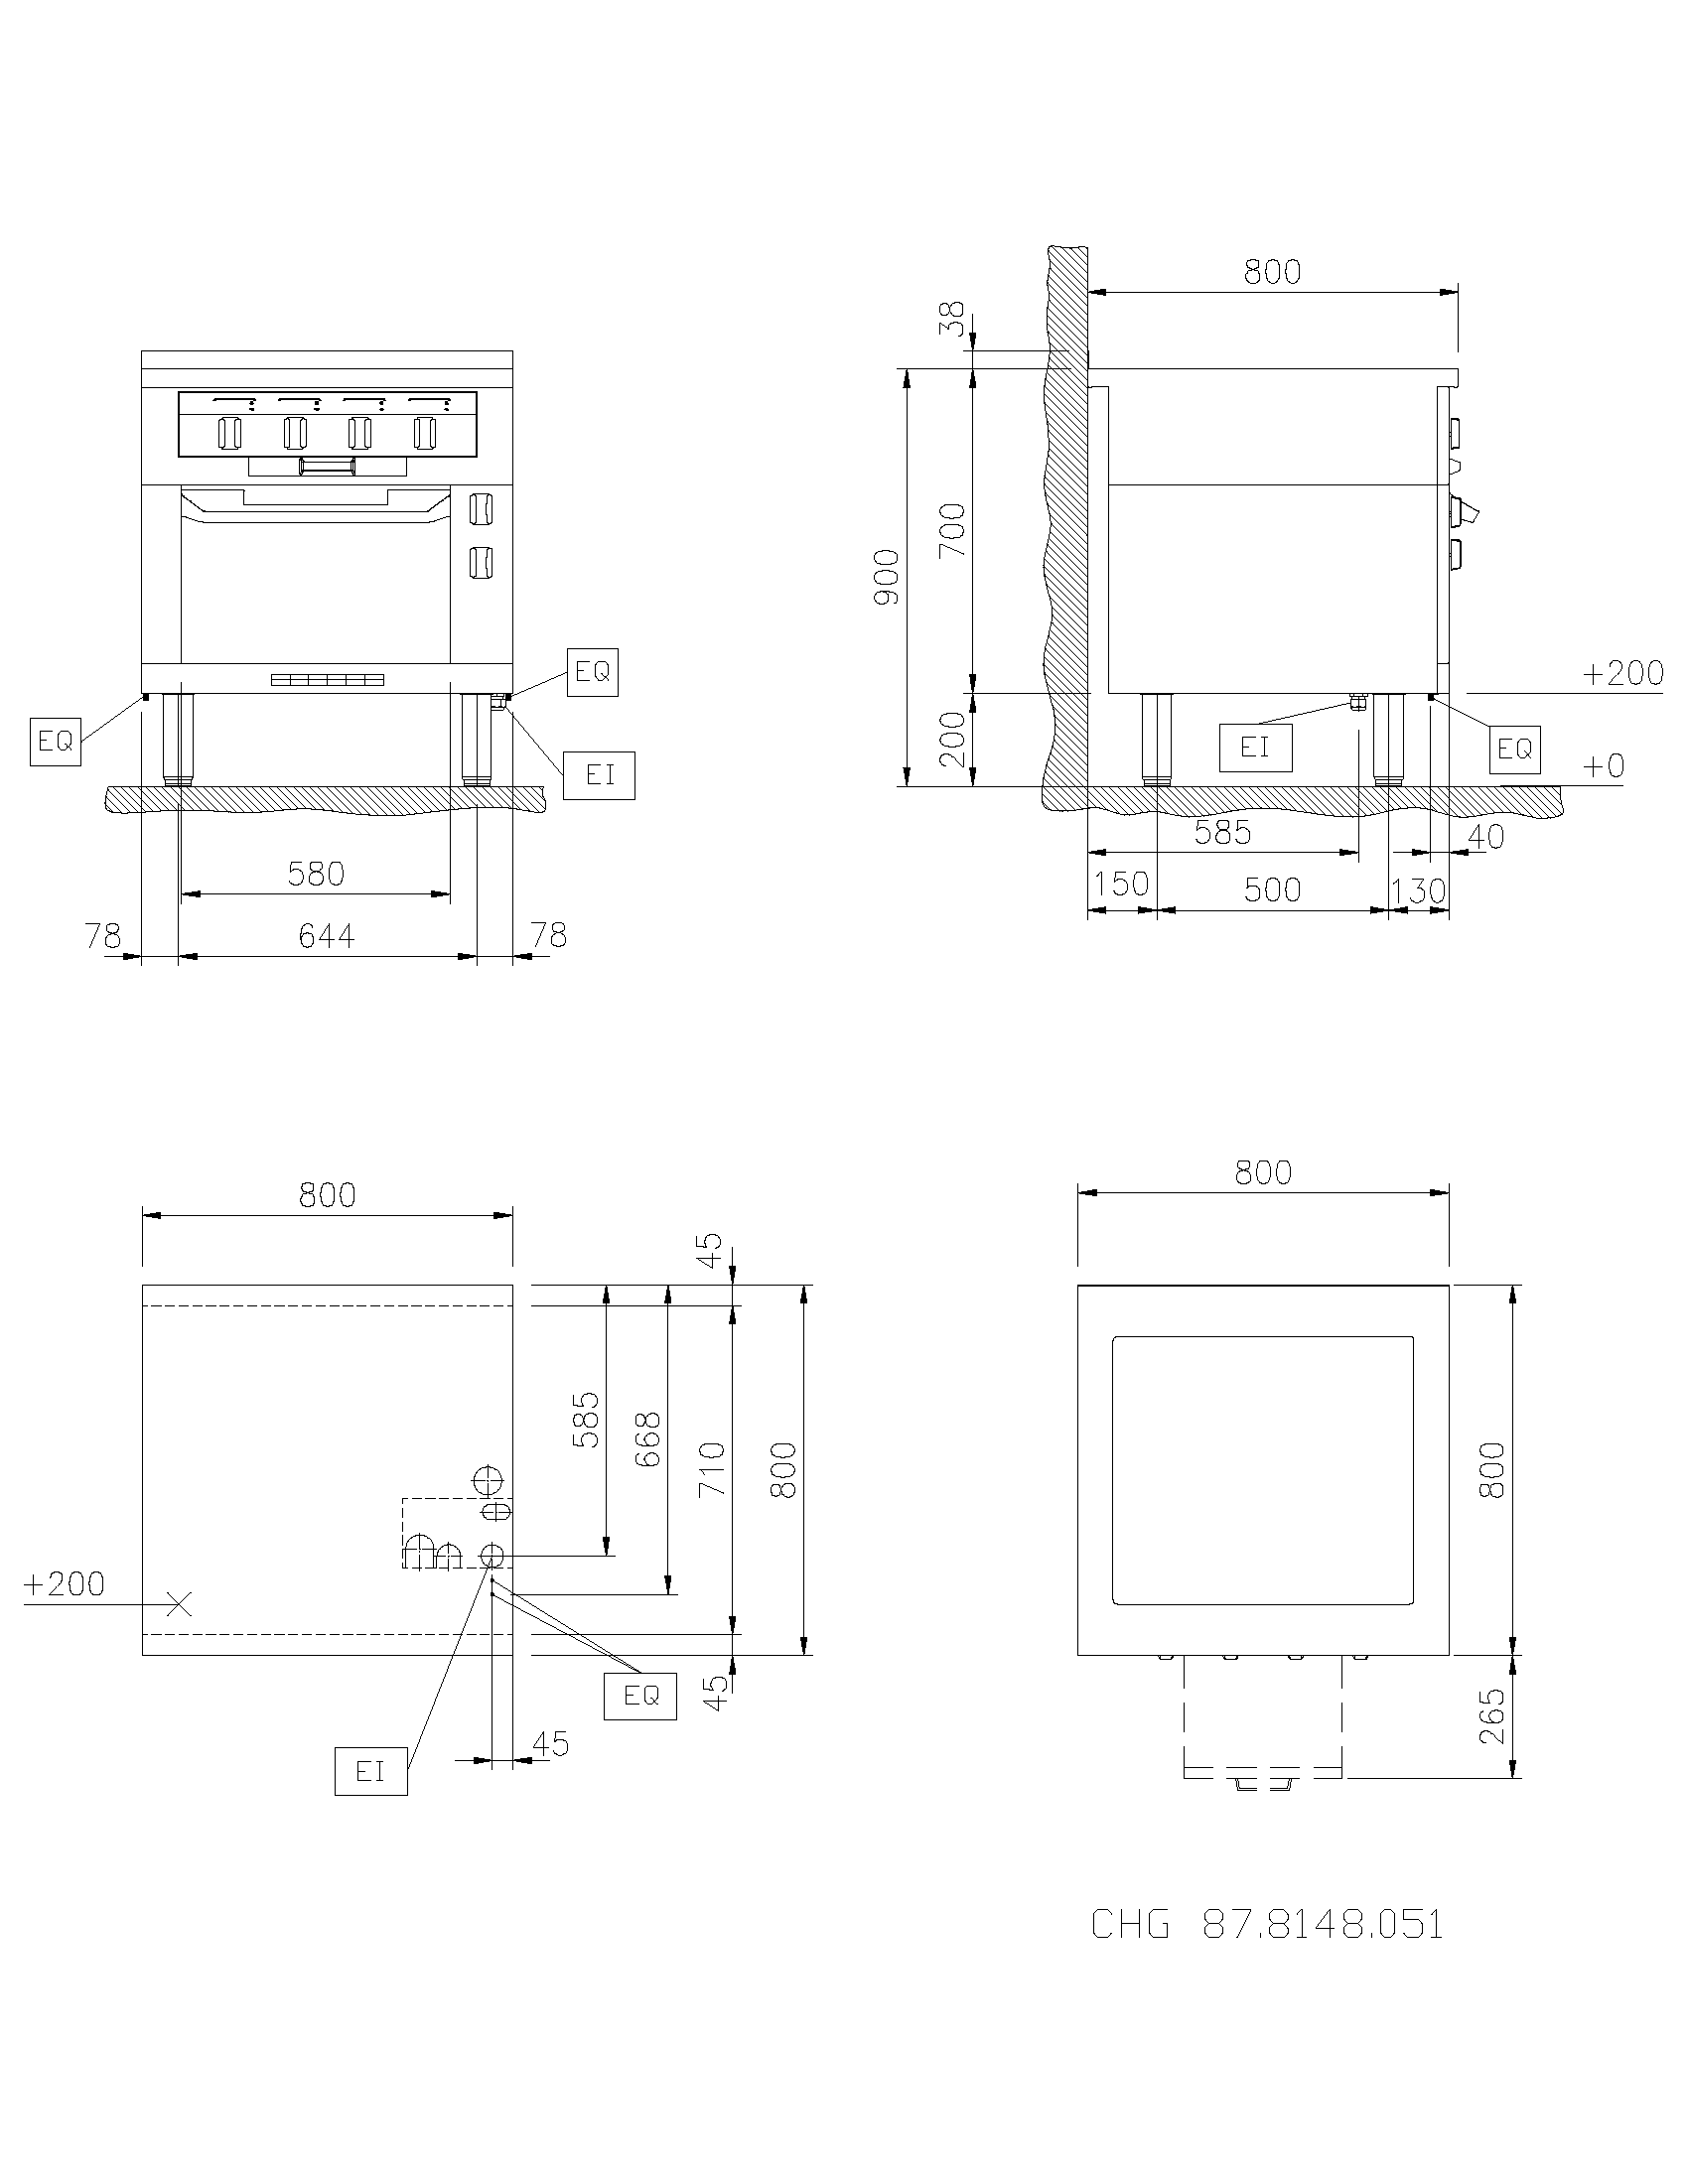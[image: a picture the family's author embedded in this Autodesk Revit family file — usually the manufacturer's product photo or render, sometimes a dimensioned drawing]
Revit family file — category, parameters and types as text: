
# Revit family: QF_ELECTROLUXPROFESSIONAL_589840_MCH2EAH1DM
name_source: partatom
category: Attrezzature speciali
units: mm (PartAtom-declared; Revit-internal decimal feet)

## family parameters
Basato su piano di lavoro = No
Condiviso = No
Punto di calcolo locali = No
Quota connettore circolare = Usa diametro
Sempre verticale = Sì
Taglio con vuoti quando caricato = No
Tipo di parte = Normale

## types (1)
- Standard
    Accessory = Sì
    Cold Water Size = 0"
    Compressed Air Pressure = 0.00 psi
    Compressed Air Size = 0"
    Compressed Air Volume = 0 GPM
    Condensate Return Size = 0"
    Cycle = 50 Hz
    Depth Actual = 900 mm  [stored 2.95276 ft]
    Descrizione = FRYTOP,H3,MXD,2Z,1S,800X900X700H MARINE
    Direct Waste Size = 0"
    Gas Input Pressure = 0.0
    Gas KW = 0
    Gas Size = 0"
    HP = 20.5 HP
    Height Actual = 700 mm  [stored 2.29659 ft]
    Hot Water Size = 0"
    Item Number = 589840
    Length Actual = 800 mm  [stored 2.62467 ft]
    Modello = MCH2EAH1DM
    Phase = 3
    Produttore = Electrolux Professional
    Prospetto di default = 0 mm  [stored 0 ft]
    Refrigerant Compressor Remote = Sì
    Refrigeration Liquid Line Size = 0 mm  [stored 0 ft]
    Refrigeration Suction Line Size = 0 mm  [stored 0 ft]
    Steam Consumption per Hour = 0
    Steam Supply Maximum Pressure = 0.00 psi
    Steam Supply Minimum Pressure = 0.00 psi
    Steam Supply Size = 0"
    URL = https://www.electroluxprofessional.com
    URL Manufacturer = https://www.electroluxprofessional.com
    Volts = 440 V
    Watts = 15300 W
    Weight = 150.00 kg

note: source unit labels omitted for Gas Input Pressure — the stored unit's dimension contradicts the parameter name (converter mislabeling)

note: [stored X ft] marks values corroborated as IEEE doubles in the binary element streams (Revit-internal decimal feet)

## geometry (parser evidence)
native form markers: Blend x13, Sweep x8
no freeform markers — native parametric forms only
